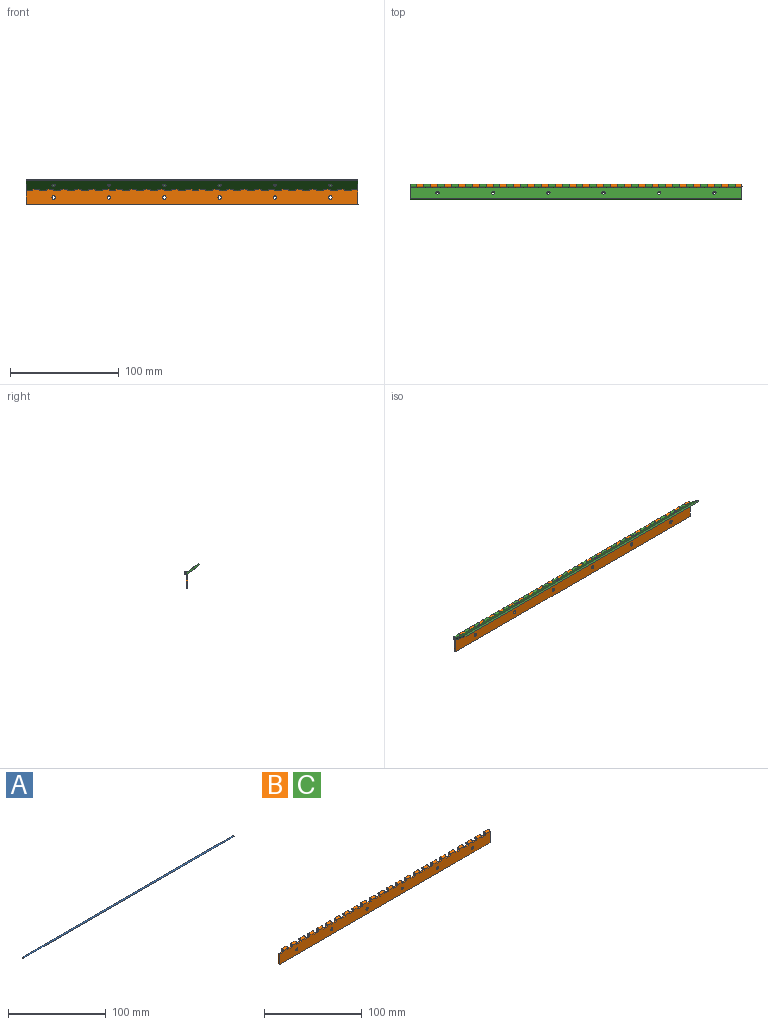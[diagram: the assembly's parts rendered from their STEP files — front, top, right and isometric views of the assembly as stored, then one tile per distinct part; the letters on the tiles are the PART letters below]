
ASSEMBLY  parts=3 mates=4
PART A: 3 faces, bbox 304.8x1.6x1.6 mm
  f0: cylinder r=0.79mm len=304.8mm, axis (-1,0,0), area 1520.1mm2, adj f1,f2
  f1: plane 1.59x1.59mm, normal (1,0,0), area 2mm2, adj f0
  f2: plane 1.59x1.59mm, normal (-1,0,0), area 2mm2, adj f0
PART B: 130 faces, bbox 304.8x3.2x15.9 mm
  f0: cylinder r=1.59mm len=6.35mm, axis (-1,0,0), area 47.5mm2, adj f23,f25,f118,f122
  f1: cylinder r=1.59mm len=6.35mm, axis (-1,0,0), area 47.5mm2, adj f23,f25,f114,f119
  f2: cylinder r=1.59mm len=6.35mm, axis (-1,0,0), area 47.5mm2, adj f23,f25,f110,f115
  f3: cylinder r=1.59mm len=6.35mm, axis (-1,0,0), area 47.5mm2, adj f23,f25,f106,f111
  f4: cylinder r=1.59mm len=6.35mm, axis (-1,0,0), area 47.5mm2, adj f23,f25,f102,f107
  f5: cylinder r=1.59mm len=6.35mm, axis (-1,0,0), area 47.5mm2, adj f23,f25,f98,f103
  f6: cylinder r=1.59mm len=6.35mm, axis (-1,0,0), area 47.5mm2, adj f23,f25,f94,f99
  f7: cylinder r=1.59mm len=6.35mm, axis (-1,0,0), area 47.5mm2, adj f23,f25,f90,f95
  f8: cylinder r=1.59mm len=6.35mm, axis (-1,0,0), area 47.5mm2, adj f23,f25,f86,f91
  f9: cylinder r=1.59mm len=6.35mm, axis (-1,0,0), area 47.5mm2, adj f23,f25,f82,f87
  f10: cylinder r=1.59mm len=6.35mm, axis (-1,0,0), area 47.5mm2, adj f23,f25,f78,f83
  f11: cylinder r=1.59mm len=6.35mm, axis (-1,0,0), area 47.5mm2, adj f23,f25,f74,f79
  f12: cylinder r=1.59mm len=6.35mm, axis (-1,0,0), area 47.5mm2, adj f23,f25,f70,f75
  f13: cylinder r=1.59mm len=6.35mm, axis (-1,0,0), area 47.5mm2, adj f23,f25,f66,f71
  f14: cylinder r=1.59mm len=6.35mm, axis (-1,0,0), area 47.5mm2, adj f23,f25,f62,f67
  f15: cylinder r=1.59mm len=6.35mm, axis (-1,0,0), area 47.5mm2, adj f23,f25,f58,f63
  f16: cylinder r=1.59mm len=6.35mm, axis (-1,0,0), area 47.5mm2, adj f23,f25,f54,f59
  f17: cylinder r=1.59mm len=6.35mm, axis (-1,0,0), area 47.5mm2, adj f23,f25,f50,f55
  f18: cylinder r=1.59mm len=6.35mm, axis (-1,0,0), area 47.5mm2, adj f23,f25,f46,f51
  f19: cylinder r=1.59mm len=6.35mm, axis (-1,0,0), area 47.5mm2, adj f23,f25,f42,f47
  f20: cylinder r=1.59mm len=6.35mm, axis (-1,0,0), area 47.5mm2, adj f23,f25,f38,f43
  f21: cylinder r=1.59mm len=6.35mm, axis (-1,0,0), area 47.5mm2, adj f23,f25,f34,f39
  f22: cylinder r=1.59mm len=6.35mm, axis (-1,0,0), area 47.5mm2, adj f23,f25,f30,f35
  f23: plane 304.8x14.29mm, normal (0,-1,0), area 4065.4mm2, adj f0,f1,f2,f3,f4,f5,f6,f7
  f24: plane 12.7x1.59mm, normal (-1,0,0), area 20.2mm2, adj f23,f25,f28,f123
  f25: plane 304.8x12.7mm, normal (0,1,0), area 3823.5mm2, adj f0,f1,f2,f3,f4,f5,f6,f7
  f26: cylinder r=1.59mm len=6.35mm, axis (-1,0,0), area 47.5mm2, adj f23,f25,f29,f31
  f27: cylinder r=0.79mm len=6.35mm, axis (-1,0,0), area 31.7mm2, adj f29,f31
  f28: plane 304.8x1.59mm, normal (0,0,-1), area 483.9mm2, adj f23,f24,f25,f29
  f29: plane 15.88x3.18mm, normal (1,0,0), area 26.6mm2, adj f23,f25,f26,f27,f28
  f30: plane 3.18x3.18mm, normal (1,0,0), area 6.5mm2, adj f22,f23,f32,f33
  f31: plane 3.18x3.18mm, normal (-1,0,0), area 6.5mm2, adj f23,f26,f27,f32
  f32: plane 6.35x1.59mm, normal (0,0,1), area 10.1mm2, adj f23,f25,f30,f31
  f33: cylinder r=0.79mm len=6.35mm, axis (-1,0,0), area 31.7mm2, adj f30,f35
  f34: plane 3.18x3.18mm, normal (1,0,0), area 6.5mm2, adj f21,f23,f36,f37
  f35: plane 3.18x3.18mm, normal (-1,0,0), area 6.5mm2, adj f22,f23,f33,f36
  f36: plane 6.35x1.59mm, normal (0,0,1), area 10.1mm2, adj f23,f25,f34,f35
  f37: cylinder r=0.79mm len=6.35mm, axis (-1,0,0), area 31.7mm2, adj f34,f39
  f38: plane 3.18x3.18mm, normal (1,0,0), area 6.5mm2, adj f20,f23,f40,f41
  f39: plane 3.18x3.18mm, normal (-1,0,0), area 6.5mm2, adj f21,f23,f37,f40
  f40: plane 6.35x1.59mm, normal (0,0,1), area 10.1mm2, adj f23,f25,f38,f39
  f41: cylinder r=0.79mm len=6.35mm, axis (-1,0,0), area 31.7mm2, adj f38,f43
  f42: plane 3.18x3.18mm, normal (1,0,0), area 6.5mm2, adj f19,f23,f44,f45
  f43: plane 3.18x3.18mm, normal (-1,0,0), area 6.5mm2, adj f20,f23,f41,f44
  f44: plane 6.35x1.59mm, normal (0,0,1), area 10.1mm2, adj f23,f25,f42,f43
  f45: cylinder r=0.79mm len=6.35mm, axis (-1,0,0), area 31.7mm2, adj f42,f47
  f46: plane 3.18x3.18mm, normal (1,0,0), area 6.5mm2, adj f18,f23,f48,f49
  f47: plane 3.18x3.18mm, normal (-1,0,0), area 6.5mm2, adj f19,f23,f45,f48
  f48: plane 6.35x1.59mm, normal (0,0,1), area 10.1mm2, adj f23,f25,f46,f47
  f49: cylinder r=0.79mm len=6.35mm, axis (-1,0,0), area 31.7mm2, adj f46,f51
  f50: plane 3.18x3.18mm, normal (1,0,0), area 6.5mm2, adj f17,f23,f52,f53
  f51: plane 3.18x3.18mm, normal (-1,0,0), area 6.5mm2, adj f18,f23,f49,f52
  f52: plane 6.35x1.59mm, normal (0,0,1), area 10.1mm2, adj f23,f25,f50,f51
  f53: cylinder r=0.79mm len=6.35mm, axis (-1,0,0), area 31.7mm2, adj f50,f55
  f54: plane 3.18x3.18mm, normal (1,0,0), area 6.5mm2, adj f16,f23,f56,f57
  f55: plane 3.18x3.18mm, normal (-1,0,0), area 6.5mm2, adj f17,f23,f53,f56
  f56: plane 6.35x1.59mm, normal (0,0,1), area 10.1mm2, adj f23,f25,f54,f55
  f57: cylinder r=0.79mm len=6.35mm, axis (-1,0,0), area 31.7mm2, adj f54,f59
  f58: plane 3.18x3.18mm, normal (1,0,0), area 6.5mm2, adj f15,f23,f60,f61
  f59: plane 3.18x3.18mm, normal (-1,0,0), area 6.5mm2, adj f16,f23,f57,f60
  f60: plane 6.35x1.59mm, normal (0,0,1), area 10.1mm2, adj f23,f25,f58,f59
  f61: cylinder r=0.79mm len=6.35mm, axis (-1,0,0), area 31.7mm2, adj f58,f63
  f62: plane 3.18x3.18mm, normal (1,0,0), area 6.5mm2, adj f14,f23,f64,f65
  f63: plane 3.18x3.18mm, normal (-1,0,0), area 6.5mm2, adj f15,f23,f61,f64
  f64: plane 6.35x1.59mm, normal (0,0,1), area 10.1mm2, adj f23,f25,f62,f63
  f65: cylinder r=0.79mm len=6.35mm, axis (-1,0,0), area 31.7mm2, adj f62,f67
  f66: plane 3.18x3.18mm, normal (1,0,0), area 6.5mm2, adj f13,f23,f68,f69
  f67: plane 3.18x3.18mm, normal (-1,0,0), area 6.5mm2, adj f14,f23,f65,f68
  f68: plane 6.35x1.59mm, normal (0,0,1), area 10.1mm2, adj f23,f25,f66,f67
  f69: cylinder r=0.79mm len=6.35mm, axis (-1,0,0), area 31.7mm2, adj f66,f71
  f70: plane 3.18x3.18mm, normal (1,0,0), area 6.5mm2, adj f12,f23,f72,f73
  f71: plane 3.18x3.18mm, normal (-1,0,0), area 6.5mm2, adj f13,f23,f69,f72
  f72: plane 6.35x1.59mm, normal (0,0,1), area 10.1mm2, adj f23,f25,f70,f71
  f73: cylinder r=0.79mm len=6.35mm, axis (-1,0,0), area 31.7mm2, adj f70,f75
  f74: plane 3.18x3.18mm, normal (1,0,0), area 6.5mm2, adj f11,f23,f76,f77
  f75: plane 3.18x3.18mm, normal (-1,0,0), area 6.5mm2, adj f12,f23,f73,f76
  f76: plane 6.35x1.59mm, normal (0,0,1), area 10.1mm2, adj f23,f25,f74,f75
  f77: cylinder r=0.79mm len=6.35mm, axis (-1,0,0), area 31.7mm2, adj f74,f79
  f78: plane 3.18x3.18mm, normal (1,0,0), area 6.5mm2, adj f10,f23,f80,f81
  f79: plane 3.18x3.18mm, normal (-1,0,0), area 6.5mm2, adj f11,f23,f77,f80
  f80: plane 6.35x1.59mm, normal (0,0,1), area 10.1mm2, adj f23,f25,f78,f79
  f81: cylinder r=0.79mm len=6.35mm, axis (-1,0,0), area 31.7mm2, adj f78,f83
  f82: plane 3.18x3.18mm, normal (1,0,0), area 6.5mm2, adj f9,f23,f84,f85
  f83: plane 3.18x3.18mm, normal (-1,0,0), area 6.5mm2, adj f10,f23,f81,f84
  f84: plane 6.35x1.59mm, normal (0,0,1), area 10.1mm2, adj f23,f25,f82,f83
  f85: cylinder r=0.79mm len=6.35mm, axis (-1,0,0), area 31.7mm2, adj f82,f87
  f86: plane 3.18x3.18mm, normal (1,0,0), area 6.5mm2, adj f8,f23,f88,f89
  f87: plane 3.18x3.18mm, normal (-1,0,0), area 6.5mm2, adj f9,f23,f85,f88
  f88: plane 6.35x1.59mm, normal (0,0,1), area 10.1mm2, adj f23,f25,f86,f87
  f89: cylinder r=0.79mm len=6.35mm, axis (-1,0,0), area 31.7mm2, adj f86,f91
  f90: plane 3.18x3.18mm, normal (1,0,0), area 6.5mm2, adj f7,f23,f92,f93
  f91: plane 3.18x3.18mm, normal (-1,0,0), area 6.5mm2, adj f8,f23,f89,f92
  f92: plane 6.35x1.59mm, normal (0,0,1), area 10.1mm2, adj f23,f25,f90,f91
  f93: cylinder r=0.79mm len=6.35mm, axis (-1,0,0), area 31.7mm2, adj f90,f95
  f94: plane 3.18x3.18mm, normal (1,0,0), area 6.5mm2, adj f6,f23,f96,f97
  f95: plane 3.18x3.18mm, normal (-1,0,0), area 6.5mm2, adj f7,f23,f93,f96
  f96: plane 6.35x1.59mm, normal (0,0,1), area 10.1mm2, adj f23,f25,f94,f95
  f97: cylinder r=0.79mm len=6.35mm, axis (-1,0,0), area 31.7mm2, adj f94,f99
  f98: plane 3.18x3.18mm, normal (1,0,0), area 6.5mm2, adj f5,f23,f100,f101
  f99: plane 3.18x3.18mm, normal (-1,0,0), area 6.5mm2, adj f6,f23,f97,f100
  f100: plane 6.35x1.59mm, normal (0,0,1), area 10.1mm2, adj f23,f25,f98,f99
  f101: cylinder r=0.79mm len=6.35mm, axis (-1,0,0), area 31.7mm2, adj f98,f103
  f102: plane 3.18x3.18mm, normal (1,0,0), area 6.5mm2, adj f4,f23,f104,f105
  f103: plane 3.18x3.18mm, normal (-1,0,0), area 6.5mm2, adj f5,f23,f101,f104
  f104: plane 6.35x1.59mm, normal (0,0,1), area 10.1mm2, adj f23,f25,f102,f103
  f105: cylinder r=0.79mm len=6.35mm, axis (-1,0,0), area 31.7mm2, adj f102,f107
  f106: plane 3.18x3.18mm, normal (1,0,0), area 6.5mm2, adj f3,f23,f108,f109
  f107: plane 3.18x3.18mm, normal (-1,0,0), area 6.5mm2, adj f4,f23,f105,f108
  f108: plane 6.35x1.59mm, normal (0,0,1), area 10.1mm2, adj f23,f25,f106,f107
  f109: cylinder r=0.79mm len=6.35mm, axis (-1,0,0), area 31.7mm2, adj f106,f111
  f110: plane 3.18x3.18mm, normal (1,0,0), area 6.5mm2, adj f2,f23,f112,f113
  f111: plane 3.18x3.18mm, normal (-1,0,0), area 6.5mm2, adj f3,f23,f109,f112
  f112: plane 6.35x1.59mm, normal (0,0,1), area 10.1mm2, adj f23,f25,f110,f111
  f113: cylinder r=0.79mm len=6.35mm, axis (-1,0,0), area 31.7mm2, adj f110,f115
  f114: plane 3.18x3.18mm, normal (1,0,0), area 6.5mm2, adj f1,f23,f116,f117
  f115: plane 3.18x3.18mm, normal (-1,0,0), area 6.5mm2, adj f2,f23,f113,f116
  f116: plane 6.35x1.59mm, normal (0,0,1), area 10.1mm2, adj f23,f25,f114,f115
  f117: cylinder r=0.79mm len=6.35mm, axis (-1,0,0), area 31.7mm2, adj f114,f119
  f118: plane 3.18x3.18mm, normal (1,0,0), area 6.5mm2, adj f0,f23,f120,f121
  f119: plane 3.18x3.18mm, normal (-1,0,0), area 6.5mm2, adj f1,f23,f117,f120
  f120: plane 6.35x1.59mm, normal (0,0,1), area 10.1mm2, adj f23,f25,f118,f119
  f121: cylinder r=0.79mm len=6.35mm, axis (-1,0,0), area 31.7mm2, adj f118,f122
  f122: plane 3.18x3.18mm, normal (-1,0,0), area 6.5mm2, adj f0,f23,f121,f123
  f123: plane 6.35x1.59mm, normal (0,0,1), area 10.1mm2, adj f23,f24,f25,f122
  f124: cylinder r=1.59mm len=3.18mm, axis (0,-1,0), area 15.8mm2, adj f23,f25
  f125: cylinder r=1.59mm len=3.18mm, axis (0,-1,0), area 15.8mm2, adj f23,f25
  f126: cylinder r=1.59mm len=3.18mm, axis (0,-1,0), area 15.8mm2, adj f23,f25
  f127: cylinder r=1.59mm len=3.18mm, axis (0,-1,0), area 15.8mm2, adj f23,f25
  f128: cylinder r=1.59mm len=3.18mm, axis (0,-1,0), area 15.8mm2, adj f23,f25
  f129: cylinder r=1.59mm len=3.18mm, axis (0,-1,0), area 15.8mm2, adj f23,f25
PART C: same geometry as B
PLACE A t=(-56.18,24.71,-89.04)mm
PLACE B t=(-56.18,23.13,-33.23)mm
PLACE C rot(axis=(0,0.89,0.45),180deg) t=(248.62,12.35,-11.61)mm
MATE cylindrical A.f0 <-> B.f0  axis (1,0,0) through (248.62,24.71,-18.94)mm
MATE cylindrical C.f0 <-> B.f0  axis (-1,0,0) through (-56.18,24.71,-18.94)mm
MATE planar C.f31 <-> B.f122  axis (1,0,0) through (-49.83,22.97,-18.62)mm
MATE planar A.f0 <-> C.f29  axis (-1,0,0) through (-56.18,24.71,-18.94)mm
